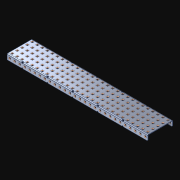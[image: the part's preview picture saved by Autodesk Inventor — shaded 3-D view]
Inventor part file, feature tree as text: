
AUTODESK INVENTOR PART (.ipt)
format: ipt  version: 2021 (Build 250183000, 183)  size: 2,269,696 bytes
history: native  units: in
note: dims shown in document units (in); Inventor stores cm internally (conversion verified against a paired STEP export)
features: extrude x197, other x197, sketch x4, pattern_linear x3
ambient origin geometry x8: Origin, YZ Plane, XZ Plane, XY Plane, X Axis, Y Axis, Z Axis, Center Point
bodies: Solid1 (feature_tree)
feature tree (401):
  pattern_linear  "Rectangular Pattern1"  Spacing1=0.182in  [1 undecoded]
  pattern_linear  "Rectangular Pattern2"  Spacing1=0.046in  [1 undecoded]
  pattern_linear  "Rectangular Pattern3"  Spacing1=0.5in  [1 undecoded]
  extrude  "Extrusion1"  Depth=0.046in
  sketch  "Sketch1"  dims[d0=0.182in]
  other  "Srf1"
  sketch  "Sketch2"  dims[d1=0.046in d2=0.0in]
  other  "Srf2"
  sketch  "Sketch3"  dims[d3=0.182in]
  other  "Srf3"
  other  "Srf4"
  other  "Srf5"
  other  "Srf6"
  other  "Srf7"
  other  "Srf8"
  other  "Srf9"
  other  "Srf10"
  other  "Srf11"
  other  "Srf12"
  other  "Srf13"
  other  "Srf14"
  other  "Srf15"
  other  "Srf16"
  other  "Srf17"
  other  "Srf18"
  other  "Srf19"
  other  "Srf20"
  other  "Srf21"
  other  "Srf22"
  other  "Srf23"
  other  "Srf24"
  other  "Srf25"
  other  "Srf26"
  other  "Srf27"
  other  "Srf28"
  other  "Srf29"
  other  "Srf30"
  other  "Srf38"
  other  "Srf39"
  other  "Srf40"
  other  "Srf41"
  other  "Srf42"
  other  "Srf43"
  other  "Srf44"
  other  "Srf45"
  other  "Srf46"
  other  "Srf47"
  other  "Srf48"
  other  "Srf49"
  other  "Srf50"
  other  "Srf51"
  other  "Srf52"
  other  "Srf53"
  other  "Srf54"
  other  "Srf55"
  other  "Srf56"
  other  "Srf57"
  other  "Srf58"
  other  "Srf59"
  other  "Srf60"
  other  "Srf61"
  other  "Srf62"
  other  "Srf63"
  other  "Srf64"
  other  "Srf72"
  other  "Srf73"
  other  "Srf74"
  other  "Srf75"
  other  "Srf76"
  other  "Srf77"
  other  "Srf78"
  other  "Srf79"
  other  "Srf80"
  other  "Srf81"
  other  "Srf82"
  other  "Srf83"
  other  "Srf84"
  other  "Srf85"
  other  "Srf86"
  other  "Srf87"
  other  "Srf88"
  other  "Srf89"
  other  "Srf90"
  other  "Srf91"
  other  "Srf92"
  other  "Srf93"
  other  "Srf94"
  other  "Srf95"
  other  "Srf96"
  other  "Srf97"
  other  "Srf98"
  other  "Srf99"
  other  "Srf107"
  other  "Srf108"
  other  "Srf109"
  other  "Srf110"
  other  "Srf111"
  other  "Srf112"
  other  "Srf113"
  other  "Srf114"
  other  "Srf115"
  other  "Srf116"
  other  "Srf117"
  other  "Srf118"
  other  "Srf119"
  other  "Srf120"
  other  "Srf121"
  other  "Srf122"
  other  "Srf123"
  other  "Srf124"
  other  "Srf125"
  other  "Srf126"
  other  "Srf127"
  other  "Srf128"
  other  "Srf129"
  other  "Srf130"
  other  "Srf131"
  other  "Srf132"
  other  "Srf133"
  other  "Srf134"
  other  "Srf142"
  other  "Srf143"
  other  "Srf144"
  other  "Srf145"
  other  "Srf146"
  other  "Srf147"
  other  "Srf148"
  other  "Srf149"
  other  "Srf150"
  other  "Srf151"
  other  "Srf152"
  other  "Srf153"
  other  "Srf154"
  other  "Srf155"
  other  "Srf156"
  other  "Srf157"
  other  "Srf158"
  other  "Srf159"
  other  "Srf160"
  other  "Srf161"
  other  "Srf162"
  other  "Srf163"
  other  "Srf164"
  other  "Srf165"
  other  "Srf166"
  other  "Srf167"
  other  "Srf168"
  other  "Srf169"
  other  "Srf177"
  other  "Srf178"
  other  "Srf179"
  other  "Srf180"
  other  "Srf181"
  other  "Srf182"
  other  "Srf183"
  other  "Srf184"
  other  "Srf185"
  other  "Srf186"
  other  "Srf187"
  other  "Srf188"
  other  "Srf189"
  other  "Srf190"
  other  "Srf191"
  other  "Srf192"
  other  "Srf193"
  other  "Srf194"
  other  "Srf195"
  other  "Srf196"
  other  "Srf197"
  other  "Srf198"
  other  "Srf199"
  other  "Srf200"
  other  "Srf201"
  other  "Srf202"
  other  "Srf203"
  other  "Srf204"
  other  "Srf212"
  other  "Srf213"
  other  "Srf214"
  other  "Srf215"
  other  "Srf216"
  other  "Srf217"
  other  "Srf218"
  other  "Srf219"
  other  "Srf220"
  other  "Srf221"
  other  "Srf222"
  other  "Srf223"
  other  "Srf224"
  other  "Srf225"
  other  "Srf226"
  other  "Srf227"
  other  "Srf228"
  other  "Srf229"
  other  "Srf230"
  other  "Srf231"
  other  "Srf232"
  other  "Srf233"
  other  "Srf234"
  other  "Srf235"
  other  "Srf236"
  other  "Srf237"
  other  "Srf238"
  sketch  "Sketch4"  dims[d4=0.046in d5=0.0in d6=0.182in d7=0.046in d8=0.0in d11=0.5in d12=11.0236in d14=0.5in d15=1.9685in d17=0.5in d18=11.0236in d20=0.5in d21=3.5in d22=0.0in]
  parser-record x1  (decoder bookkeeping rows leaked as tree rows — omitted from the tree; the rows remain in map.json)
  extrude  "ExtrusionSrf1"  Depth=0.046in
  extrude  "ExtrusionSrf2"  Depth=0.046in
  extrude  "ExtrusionSrf3"  Depth=0.046in
  extrude  "ExtrusionSrf4"  Depth=0.046in
  extrude  "ExtrusionSrf5"  Depth=0.046in
  extrude  "ExtrusionSrf6"  TaperAngle=0.0deg  [1 undecoded]
  extrude  "ExtrusionSrf7"  [1 undecoded]
  extrude  "ExtrusionSrf8"  [1 undecoded]
  extrude  "ExtrusionSrf9"  [1 undecoded]
  extrude  "ExtrusionSrf10"  [1 undecoded]
  extrude  "ExtrusionSrf11"  [1 undecoded]
  extrude  "ExtrusionSrf12"  [1 undecoded]
  extrude  "ExtrusionSrf13"  [1 undecoded]
  extrude  "ExtrusionSrf14"  [1 undecoded]
  extrude  "ExtrusionSrf15"  [1 undecoded]
  extrude  "ExtrusionSrf16"  [1 undecoded]
  extrude  "ExtrusionSrf17"  [1 undecoded]
  extrude  "ExtrusionSrf18"  [1 undecoded]
  extrude  "ExtrusionSrf19"  [1 undecoded]
  extrude  "ExtrusionSrf20"  [1 undecoded]
  extrude  "ExtrusionSrf21"  [1 undecoded]
  extrude  "ExtrusionSrf22"  [1 undecoded]
  extrude  "ExtrusionSrf23"  [1 undecoded]
  extrude  "ExtrusionSrf24"  [1 undecoded]
  extrude  "ExtrusionSrf25"  [1 undecoded]
  extrude  "ExtrusionSrf26"  [1 undecoded]
  extrude  "ExtrusionSrf27"  [1 undecoded]
  extrude  "ExtrusionSrf28"  [1 undecoded]
  extrude  "ExtrusionSrf29"  [1 undecoded]
  extrude  "ExtrusionSrf30"  [1 undecoded]
  extrude  "ExtrusionSrf38"  [1 undecoded]
  extrude  "ExtrusionSrf39"  [1 undecoded]
  extrude  "ExtrusionSrf40"  [1 undecoded]
  extrude  "ExtrusionSrf41"  [1 undecoded]
  extrude  "ExtrusionSrf42"  [1 undecoded]
  extrude  "ExtrusionSrf43"  [1 undecoded]
  extrude  "ExtrusionSrf44"  [1 undecoded]
  extrude  "ExtrusionSrf45"  [1 undecoded]
  extrude  "ExtrusionSrf46"  [1 undecoded]
  extrude  "ExtrusionSrf47"  [1 undecoded]
  extrude  "ExtrusionSrf48"  [1 undecoded]
  extrude  "ExtrusionSrf49"  [1 undecoded]
  extrude  "ExtrusionSrf50"  [1 undecoded]
  extrude  "ExtrusionSrf51"  [1 undecoded]
  extrude  "ExtrusionSrf52"  [1 undecoded]
  extrude  "ExtrusionSrf53"  [1 undecoded]
  extrude  "ExtrusionSrf54"  [1 undecoded]
  extrude  "ExtrusionSrf55"  [1 undecoded]
  extrude  "ExtrusionSrf56"  [1 undecoded]
  extrude  "ExtrusionSrf57"  [1 undecoded]
  extrude  "ExtrusionSrf58"  [1 undecoded]
  extrude  "ExtrusionSrf59"  [1 undecoded]
  extrude  "ExtrusionSrf60"  [1 undecoded]
  extrude  "ExtrusionSrf61"  [1 undecoded]
  extrude  "ExtrusionSrf62"  [1 undecoded]
  extrude  "ExtrusionSrf63"  [1 undecoded]
  extrude  "ExtrusionSrf64"  [1 undecoded]
  extrude  "ExtrusionSrf72"  [1 undecoded]
  extrude  "ExtrusionSrf73"  [1 undecoded]
  extrude  "ExtrusionSrf74"  [1 undecoded]
  extrude  "ExtrusionSrf75"  [1 undecoded]
  extrude  "ExtrusionSrf76"  [1 undecoded]
  extrude  "ExtrusionSrf77"  [1 undecoded]
  extrude  "ExtrusionSrf78"  [1 undecoded]
  extrude  "ExtrusionSrf79"  [1 undecoded]
  extrude  "ExtrusionSrf80"  [1 undecoded]
  extrude  "ExtrusionSrf81"  [1 undecoded]
  extrude  "ExtrusionSrf82"  [1 undecoded]
  extrude  "ExtrusionSrf83"  [1 undecoded]
  extrude  "ExtrusionSrf84"  [1 undecoded]
  extrude  "ExtrusionSrf85"  [1 undecoded]
  extrude  "ExtrusionSrf86"  [1 undecoded]
  extrude  "ExtrusionSrf87"  [1 undecoded]
  extrude  "ExtrusionSrf88"  [1 undecoded]
  extrude  "ExtrusionSrf89"  [1 undecoded]
  extrude  "ExtrusionSrf90"  [1 undecoded]
  extrude  "ExtrusionSrf91"  [1 undecoded]
  extrude  "ExtrusionSrf92"  [1 undecoded]
  extrude  "ExtrusionSrf93"  [1 undecoded]
  extrude  "ExtrusionSrf94"  [1 undecoded]
  extrude  "ExtrusionSrf95"  [1 undecoded]
  extrude  "ExtrusionSrf96"  [1 undecoded]
  extrude  "ExtrusionSrf97"  [1 undecoded]
  extrude  "ExtrusionSrf98"  [1 undecoded]
  extrude  "ExtrusionSrf99"  [1 undecoded]
  extrude  "ExtrusionSrf107"  [1 undecoded]
  extrude  "ExtrusionSrf108"  [1 undecoded]
  extrude  "ExtrusionSrf109"  [1 undecoded]
  extrude  "ExtrusionSrf110"  [1 undecoded]
  extrude  "ExtrusionSrf111"  [1 undecoded]
  extrude  "ExtrusionSrf112"  [1 undecoded]
  extrude  "ExtrusionSrf113"  [1 undecoded]
  extrude  "ExtrusionSrf114"  [1 undecoded]
  extrude  "ExtrusionSrf115"  [1 undecoded]
  extrude  "ExtrusionSrf116"  [1 undecoded]
  extrude  "ExtrusionSrf117"  [1 undecoded]
  extrude  "ExtrusionSrf118"  [1 undecoded]
  extrude  "ExtrusionSrf119"  [1 undecoded]
  extrude  "ExtrusionSrf120"  [1 undecoded]
  extrude  "ExtrusionSrf121"  [1 undecoded]
  extrude  "ExtrusionSrf122"  [1 undecoded]
  extrude  "ExtrusionSrf123"  [1 undecoded]
  extrude  "ExtrusionSrf124"  [1 undecoded]
  extrude  "ExtrusionSrf125"  [1 undecoded]
  extrude  "ExtrusionSrf126"  [1 undecoded]
  extrude  "ExtrusionSrf127"  [1 undecoded]
  extrude  "ExtrusionSrf128"  [1 undecoded]
  extrude  "ExtrusionSrf129"  [1 undecoded]
  extrude  "ExtrusionSrf130"  [1 undecoded]
  extrude  "ExtrusionSrf131"  [1 undecoded]
  extrude  "ExtrusionSrf132"  [1 undecoded]
  extrude  "ExtrusionSrf133"  [1 undecoded]
  extrude  "ExtrusionSrf134"  [1 undecoded]
  extrude  "ExtrusionSrf142"  [1 undecoded]
  extrude  "ExtrusionSrf143"  [1 undecoded]
  extrude  "ExtrusionSrf144"  [1 undecoded]
  extrude  "ExtrusionSrf145"  [1 undecoded]
  extrude  "ExtrusionSrf146"  [1 undecoded]
  extrude  "ExtrusionSrf147"  [1 undecoded]
  extrude  "ExtrusionSrf148"  [1 undecoded]
  extrude  "ExtrusionSrf149"  [1 undecoded]
  extrude  "ExtrusionSrf150"  [1 undecoded]
  extrude  "ExtrusionSrf151"  [1 undecoded]
  extrude  "ExtrusionSrf152"  [1 undecoded]
  extrude  "ExtrusionSrf153"  [1 undecoded]
  extrude  "ExtrusionSrf154"  [1 undecoded]
  extrude  "ExtrusionSrf155"  [1 undecoded]
  extrude  "ExtrusionSrf156"  [1 undecoded]
  extrude  "ExtrusionSrf157"  [1 undecoded]
  extrude  "ExtrusionSrf158"  [1 undecoded]
  extrude  "ExtrusionSrf159"  [1 undecoded]
  extrude  "ExtrusionSrf160"  [1 undecoded]
  extrude  "ExtrusionSrf161"  [1 undecoded]
  extrude  "ExtrusionSrf162"  [1 undecoded]
  extrude  "ExtrusionSrf163"  [1 undecoded]
  extrude  "ExtrusionSrf164"  [1 undecoded]
  extrude  "ExtrusionSrf165"  [1 undecoded]
  extrude  "ExtrusionSrf166"  [1 undecoded]
  extrude  "ExtrusionSrf167"  [1 undecoded]
  extrude  "ExtrusionSrf168"  [1 undecoded]
  extrude  "ExtrusionSrf169"  [1 undecoded]
  extrude  "ExtrusionSrf177"  [1 undecoded]
  extrude  "ExtrusionSrf178"  [1 undecoded]
  extrude  "ExtrusionSrf179"  [1 undecoded]
  extrude  "ExtrusionSrf180"  [1 undecoded]
  extrude  "ExtrusionSrf181"  [1 undecoded]
  extrude  "ExtrusionSrf182"  [1 undecoded]
  extrude  "ExtrusionSrf183"  [1 undecoded]
  extrude  "ExtrusionSrf184"  [1 undecoded]
  extrude  "ExtrusionSrf185"  [1 undecoded]
  extrude  "ExtrusionSrf186"  [1 undecoded]
  extrude  "ExtrusionSrf187"  [1 undecoded]
  extrude  "ExtrusionSrf188"  [1 undecoded]
  extrude  "ExtrusionSrf189"  [1 undecoded]
  extrude  "ExtrusionSrf190"  [1 undecoded]
  extrude  "ExtrusionSrf191"  [1 undecoded]
  extrude  "ExtrusionSrf192"  [1 undecoded]
  extrude  "ExtrusionSrf193"  [1 undecoded]
  extrude  "ExtrusionSrf194"  [1 undecoded]
  extrude  "ExtrusionSrf195"  [1 undecoded]
  extrude  "ExtrusionSrf196"  [1 undecoded]
  extrude  "ExtrusionSrf197"  [1 undecoded]
  extrude  "ExtrusionSrf198"  [1 undecoded]
  extrude  "ExtrusionSrf199"  [1 undecoded]
  extrude  "ExtrusionSrf200"  [1 undecoded]
  extrude  "ExtrusionSrf201"  [1 undecoded]
  extrude  "ExtrusionSrf202"  [1 undecoded]
  extrude  "ExtrusionSrf203"  [1 undecoded]
  extrude  "ExtrusionSrf204"  [1 undecoded]
  extrude  "ExtrusionSrf212"  [1 undecoded]
  extrude  "ExtrusionSrf213"  [1 undecoded]
  extrude  "ExtrusionSrf214"  [1 undecoded]
  extrude  "ExtrusionSrf215"  [1 undecoded]
  extrude  "ExtrusionSrf216"  [1 undecoded]
  extrude  "ExtrusionSrf217"  [1 undecoded]
  extrude  "ExtrusionSrf218"  [1 undecoded]
  extrude  "ExtrusionSrf219"  [1 undecoded]
  extrude  "ExtrusionSrf220"  [1 undecoded]
  extrude  "ExtrusionSrf221"  [1 undecoded]
  extrude  "ExtrusionSrf222"  [1 undecoded]
  extrude  "ExtrusionSrf223"  [1 undecoded]
  extrude  "ExtrusionSrf224"  [1 undecoded]
  extrude  "ExtrusionSrf225"  [1 undecoded]
  extrude  "ExtrusionSrf226"  [1 undecoded]
  extrude  "ExtrusionSrf227"  [1 undecoded]
  extrude  "ExtrusionSrf228"  [1 undecoded]
  extrude  "ExtrusionSrf229"  [1 undecoded]
  extrude  "ExtrusionSrf230"  [1 undecoded]
  extrude  "ExtrusionSrf231"  [1 undecoded]
  extrude  "ExtrusionSrf232"  [1 undecoded]
  extrude  "ExtrusionSrf233"  [1 undecoded]
  extrude  "ExtrusionSrf234"  [1 undecoded]
  extrude  "ExtrusionSrf235"  [1 undecoded]
  extrude  "ExtrusionSrf236"  [1 undecoded]
  extrude  "ExtrusionSrf237"  [1 undecoded]
  extrude  "ExtrusionSrf238"  [1 undecoded]
note: 194 required parameter values undecoded (feature->parameter linkage not recoverable at this tier; creation-order binding heuristic only, values carry confidence <= 0.55)
